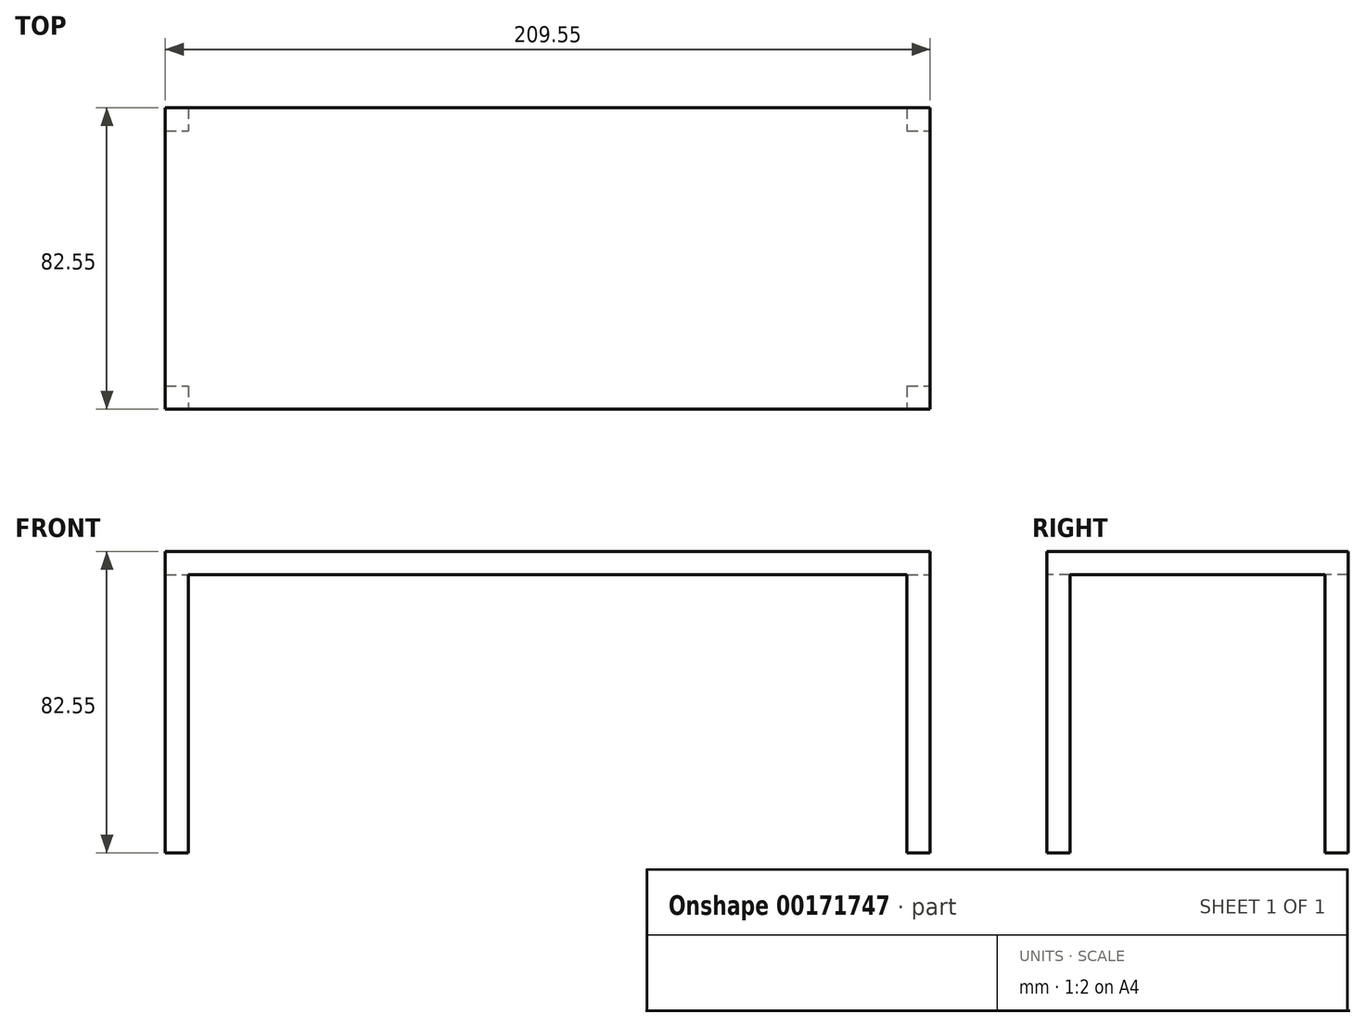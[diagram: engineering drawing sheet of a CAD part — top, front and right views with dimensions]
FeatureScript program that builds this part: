
annotation { "Feature Type Name" : "Feature", "Feature Type Description" : "" }
export const myFeature = defineFeature(function(context is Context, id is Id, definition is map)
    precondition{}
    {
        {
            var Q0;
            Q0=qCreatedBy(makeId("Top.planeOp"),FACE);
            var sketch = newSketch(context, id + "F0", { "sketchPlane" : qUnion([Q0])});
            skLineSegment(sketch, "E0.bottom", {"start": v(0, 0) * mm, "end": v(6.35, 0) * mm});
            skLineSegment(sketch, "E0.top", {"start": v(0, -6.35) * mm, "end": v(6.35, -6.35) * mm});
            skLineSegment(sketch, "E0.left", {"start": v(0, 0) * mm, "end": v(0, -6.35) * mm});
            skLineSegment(sketch, "E0.right", {"start": v(6.35, 0) * mm, "end": v(6.35, -6.35) * mm});
            skLineSegment(sketch, "E1.0.1.0", {"start": v(0, 76.2) * mm, "end": v(0, 69.85) * mm});
            skLineSegment(sketch, "E1.0.1.1", {"start": v(6.35, 76.2) * mm, "end": v(6.35, 69.85) * mm});
            skLineSegment(sketch, "E1.0.1.2", {"start": v(0, 76.2) * mm, "end": v(6.35, 76.2) * mm});
            skLineSegment(sketch, "E1.0.1.3", {"start": v(0, 69.85) * mm, "end": v(6.35, 69.85) * mm});
            skLineSegment(sketch, "E1.1.0.0", {"start": v(203.2, 0) * mm, "end": v(203.2, -6.35) * mm});
            skLineSegment(sketch, "E1.1.0.1", {"start": v(209.55, 0) * mm, "end": v(209.55, -6.35) * mm});
            skLineSegment(sketch, "E1.1.0.2", {"start": v(203.2, 0) * mm, "end": v(209.55, 0) * mm});
            skLineSegment(sketch, "E1.1.0.3", {"start": v(203.2, -6.35) * mm, "end": v(209.55, -6.35) * mm});
            skLineSegment(sketch, "E1.1.1.0", {"start": v(203.2, 76.2) * mm, "end": v(203.2, 69.85) * mm});
            skLineSegment(sketch, "E1.1.1.1", {"start": v(209.55, 76.2) * mm, "end": v(209.55, 69.85) * mm});
            skLineSegment(sketch, "E1.1.1.2", {"start": v(203.2, 76.2) * mm, "end": v(209.55, 76.2) * mm});
            skLineSegment(sketch, "E1.1.1.3", {"start": v(203.2, 69.85) * mm, "end": v(209.55, 69.85) * mm});
            skLineSegment(sketch, "E1.direction1", {"start": v(0, -6.35) * mm, "end": v(203.2, -6.35) * mm, "construction": true});
            skLineSegment(sketch, "E1.direction2", {"start": v(0, -6.35) * mm, "end": v(0, 69.85) * mm, "construction": true});
            skSolve(sketch);
        }
        {
            var Q0;
            Q0 = qSketchRegion(id + "F0", true);
            extrude(context, id + "F1", {"entities" : qUnion([Q0]), "depth" : 76.2 * mm});
        }
        {
            var Q0;
            Q0=makeQuery(id+"F1.opExtrude","CAP_FACE",FACE,{"disambiguationData":[OSD([sQuery(id+"F0.wireOp",EDGE,"E1.1.1.0"),sQuery(id+"F0.wireOp",EDGE,"E1.1.1.1"),sQuery(id+"F0.wireOp",EDGE,"E1.1.1.2"),sQuery(id+"F0.wireOp",EDGE,"E1.1.1.3")])],"isStart":false});
            var sketch = newSketch(context, id + "F2", { "sketchPlane" : qUnion([Q0])});
            skPoint(sketch, "E2.firstSnap0", {"position": v(206.38, 76.2) * mm});
            skLineSegment(sketch, "E2.bottom", {"start": v(0, 76.2) * mm, "end": v(209.55, 76.2) * mm});
            skLineSegment(sketch, "E2.top", {"start": v(0, -6.35) * mm, "end": v(209.55, -6.35) * mm});
            skLineSegment(sketch, "E2.left", {"start": v(0, 76.2) * mm, "end": v(0, -6.35) * mm});
            skLineSegment(sketch, "E2.right", {"start": v(209.55, 76.2) * mm, "end": v(209.55, -6.35) * mm});
            skSolve(sketch);
        }
        {
            var Q0;
            Q0 = qSketchRegion(id + "F2", true);
            extrude(context, id + "F3", {"entities" : qUnion([Q0]), "operationType" : NewBodyOperationType.ADD, "depth" : 6.35 * mm});
        }
    });
